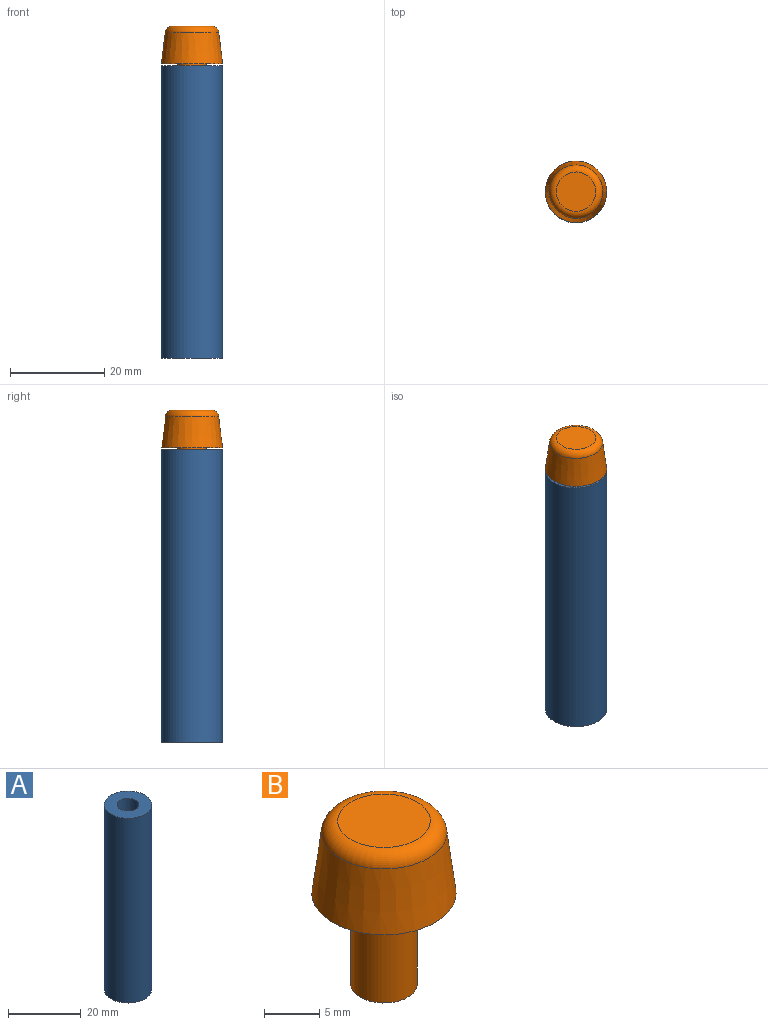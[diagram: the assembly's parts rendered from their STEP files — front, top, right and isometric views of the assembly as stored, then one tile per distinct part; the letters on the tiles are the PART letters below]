
ASSEMBLY  parts=2 mates=1
PART A: 4 faces, bbox 13x13x62 mm
  f0: cylinder r=3mm len=62mm, axis (0,0,-1), area 1168.7mm2, adj f2,f3
  f1: cylinder r=6.5mm len=62mm, axis (0,0,-1), area 2532.1mm2, adj f2,f3
  f2: plane 13x13mm, normal (0,0,1), area 104.5mm2, adj f0,f1
  f3: plane 13x13mm, normal (0,0,-1), area 104.5mm2, adj f0,f1
PART B: 6 faces, bbox 13x13x18 mm
  f0: plane 13x13mm, normal (0,0,-1), area 104.5mm2, adj f1,f4
  f1: cone r=5.66mm half-angle=7.1deg, axis (0,0,-1), area 257.5mm2, adj f0,f2
  f2: torus R=4.18mm, axis (0,0,-1), area 69.3mm2, adj f1,f3
  f3: plane 8.35x8.35mm, normal (0,0,1), area 54.8mm2, adj f2
  f4: cylinder r=3mm len=10mm, axis (0,0,1), area 188.5mm2, adj f0,f5
  f5: plane 6x6mm, normal (0,0,-1), area 28.3mm2, adj f4
PLACE A t=(-10.45,1.56,-9.92)mm fixed
PLACE B t=(-10.45,1.56,52.49)mm
MATE slider A.f1 <-> B.f4  axis (0,0,1) through (-10.45,1.56,52.08)mm
